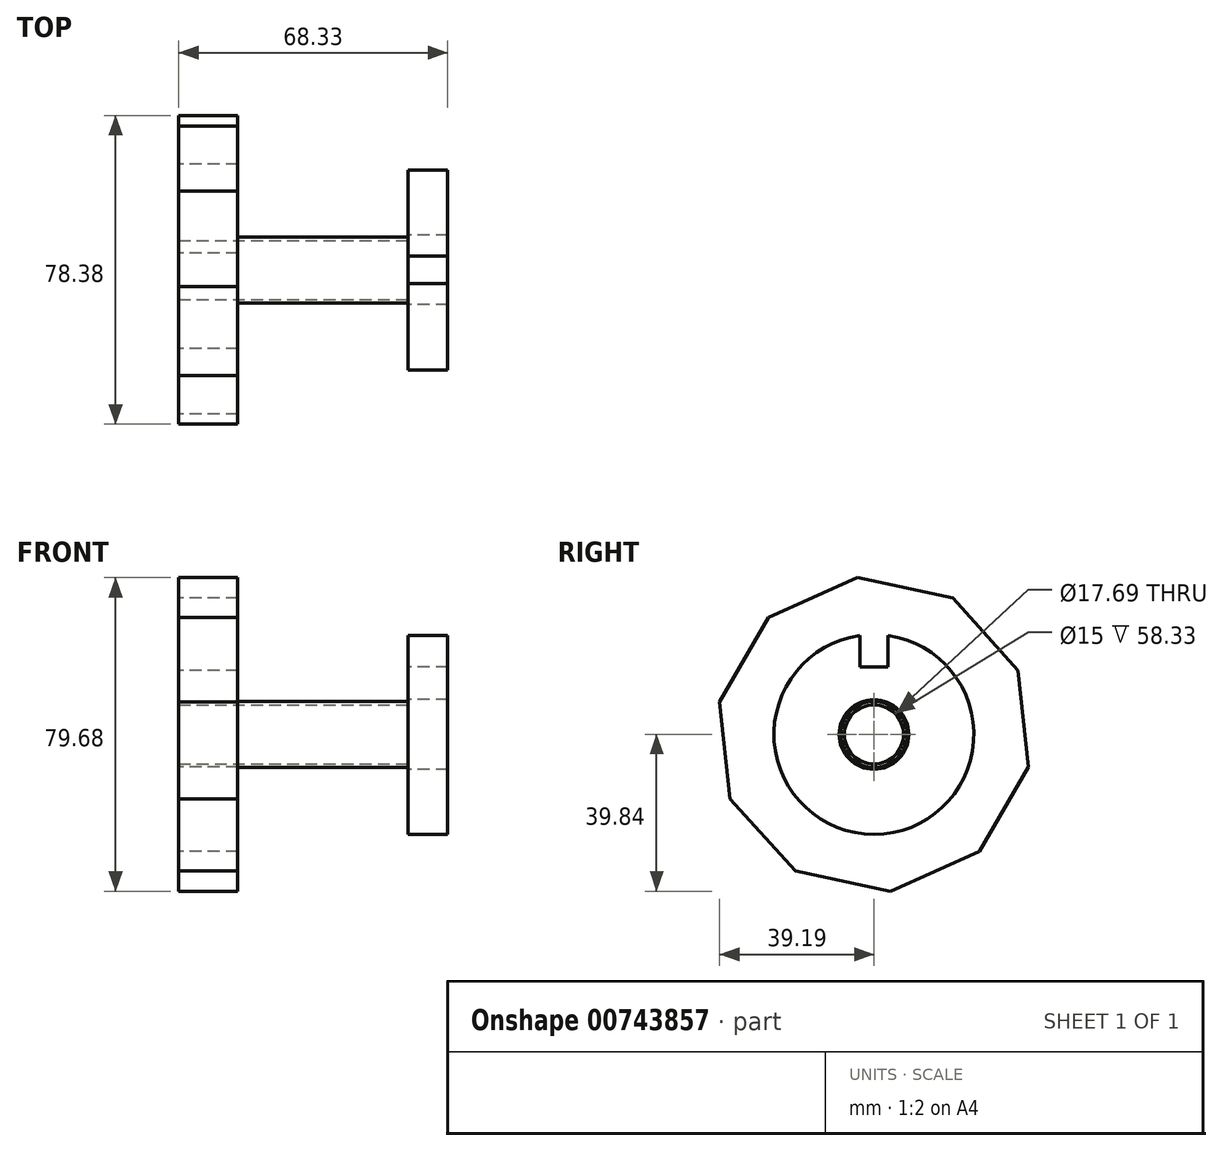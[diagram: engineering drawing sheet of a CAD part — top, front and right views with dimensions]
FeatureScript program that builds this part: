
annotation { "Feature Type Name" : "Feature", "Feature Type Description" : "" }
export const myFeature = defineFeature(function(context is Context, id is Id, definition is map)
    precondition{}
    {
        {
            var Q0;
            Q0=qCreatedBy(makeId("Right.planeOp"),FACE);
            var sketch = newSketch(context, id + "F0", { "sketchPlane" : qUnion([Q0])});
            skCircle(sketch, "E0.cCircle", {"center": v(0, 0) * mm, "radius": 38.1 * mm, "construction": true});
            skLineSegment(sketch, "E0.0", {"start": v(39.2, -8.3) * mm, "end": v(26.83, -29.75) * mm});
            skLineSegment(sketch, "E0.1", {"start": v(26.83, -29.75) * mm, "end": v(4.22, -39.84) * mm});
            skLineSegment(sketch, "E0.2", {"start": v(4.22, -39.84) * mm, "end": v(-20, -34.7) * mm});
            skLineSegment(sketch, "E0.3", {"start": v(-20, -34.7) * mm, "end": v(-36.58, -16.32) * mm});
            skLineSegment(sketch, "E0.4", {"start": v(-36.58, -16.32) * mm, "end": v(-39.2, 8.3) * mm});
            skLineSegment(sketch, "E0.5", {"start": v(-39.2, 8.3) * mm, "end": v(-26.83, 29.75) * mm});
            skLineSegment(sketch, "E0.6", {"start": v(-26.83, 29.75) * mm, "end": v(-4.22, 39.84) * mm});
            skLineSegment(sketch, "E0.7", {"start": v(-4.22, 39.84) * mm, "end": v(20, 34.7) * mm});
            skLineSegment(sketch, "E0.8", {"start": v(20, 34.7) * mm, "end": v(36.58, 16.32) * mm});
            skLineSegment(sketch, "E0.9", {"start": v(36.58, 16.32) * mm, "end": v(39.2, -8.3) * mm});
            skPoint(sketch, "E0.0.midPoint", {"position": v(33.01, -19.02) * mm});
            skSolve(sketch);
        }
        {
            var Q0;
            Q0=makeQuery(id+"F0.imprint","IMPRINT",FACE,{"disambiguationData":[TD([[makeQuery(id+"F0.imprint","IMPRINT",EDGE,{"derivedFrom":sQuery(id+"F0.wireOp",EDGE,"E0.0")}),-1.0]])]});
            extrude(context, id + "F1", {"entities" : qUnion([Q0]), "depth" : 15 * mm, "offsetDistance" : 25.4 * mm});
        }
        {
            var Q0;
            Q0=makeQuery(id+"F1.opExtrude","CAP_FACE",FACE,{"disambiguationData":[OSD([sQuery(id+"F0.wireOp",EDGE,"E0.0"),sQuery(id+"F0.wireOp",EDGE,"E0.1"),sQuery(id+"F0.wireOp",EDGE,"E0.2"),sQuery(id+"F0.wireOp",EDGE,"E0.3"),sQuery(id+"F0.wireOp",EDGE,"E0.4"),sQuery(id+"F0.wireOp",EDGE,"E0.5"),sQuery(id+"F0.wireOp",EDGE,"E0.6"),sQuery(id+"F0.wireOp",EDGE,"E0.7"),sQuery(id+"F0.wireOp",EDGE,"E0.8"),sQuery(id+"F0.wireOp",EDGE,"E0.9")])],"isStart":false});
            var sketch = newSketch(context, id + "F2", { "sketchPlane" : qUnion([Q0])});
            skCircle(sketch, "E1", {"center": v(0, 0) * mm, "radius": 7.5 * mm});
            skCircle(sketch, "E2", {"center": v(0, 0) * mm, "radius": 8.39 * mm});
            skSolve(sketch);
        }
        {
            var Q0;
            Q0=makeQuery(id+"F2.imprint","IMPRINT",FACE,{"disambiguationData":[TD([[makeQuery(id+"F2.imprint","IMPRINT",EDGE,{"derivedFrom":sQuery(id+"F2.wireOp",EDGE,"E1")}),1.0]])]});
            extrude(context, id + "F3", {"entities" : qUnion([Q0]), "operationType" : NewBodyOperationType.REMOVE, "oppositeDirection" : true, "depth" : 25.4 * mm, "offsetDistance" : 25.4 * mm});
        }
        {
            var Q0;
            Q0=makeQuery(id+"F2.imprint","IMPRINT",FACE,{"disambiguationData":[TD([[makeQuery(id+"F2.imprint","IMPRINT",EDGE,{"derivedFrom":sQuery(id+"F2.wireOp",EDGE,"E1")}),-1.0]])]});
            extrude(context, id + "F4", {"entities" : qUnion([Q0]), "operationType" : NewBodyOperationType.ADD, "depth" : 43.33 * mm, "offsetDistance" : 25.4 * mm});
        }
        {
            var Q0;
            Q0=makeQuery(id+"F4.opExtrude","CAP_FACE",FACE,{"disambiguationData":[OSD([sQuery(id+"F2.wireOp",EDGE,"E1"),sQuery(id+"F2.wireOp",EDGE,"E2")])],"isStart":false});
            var sketch = newSketch(context, id + "F5", { "sketchPlane" : qUnion([Q0])});
            skCircle(sketch, "E3", {"center": v(0, 0) * mm, "radius": 25.4 * mm});
            skLineSegment(sketch, "E4", {"start": v(-3.5, 25.16) * mm, "end": v(-3.5, 17.16) * mm});
            skLineSegment(sketch, "E5", {"start": v(-3.5, 17.16) * mm, "end": v(3.5, 17.16) * mm});
            skLineSegment(sketch, "E6", {"start": v(3.5, 17.16) * mm, "end": v(3.5, 25.16) * mm});
            skCircle(sketch, "E7", {"center": v(0, 0) * mm, "radius": 8.35 * mm});
            skCircle(sketch, "E8.0", {"center": v(0, 0) * mm, "radius": 8.85 * mm});
            skSolve(sketch);
        }
        {
            var Q0;
            {var subQ1=sQuery(id+"F5.wireOp",EDGE,"E4");Q0=makeQuery(id+"F5.imprint","IMPRINT",FACE,{"disambiguationData":[TD([[makeQuery(id+"F5.imprint","IMPRINT",EDGE,{"derivedFrom":subQ1}),-1.0]])]});}
            extrude(context, id + "F6", {"entities" : qUnion([Q0]), "depth" : 10 * mm, "offsetDistance" : 25.4 * mm});
        }
    });
